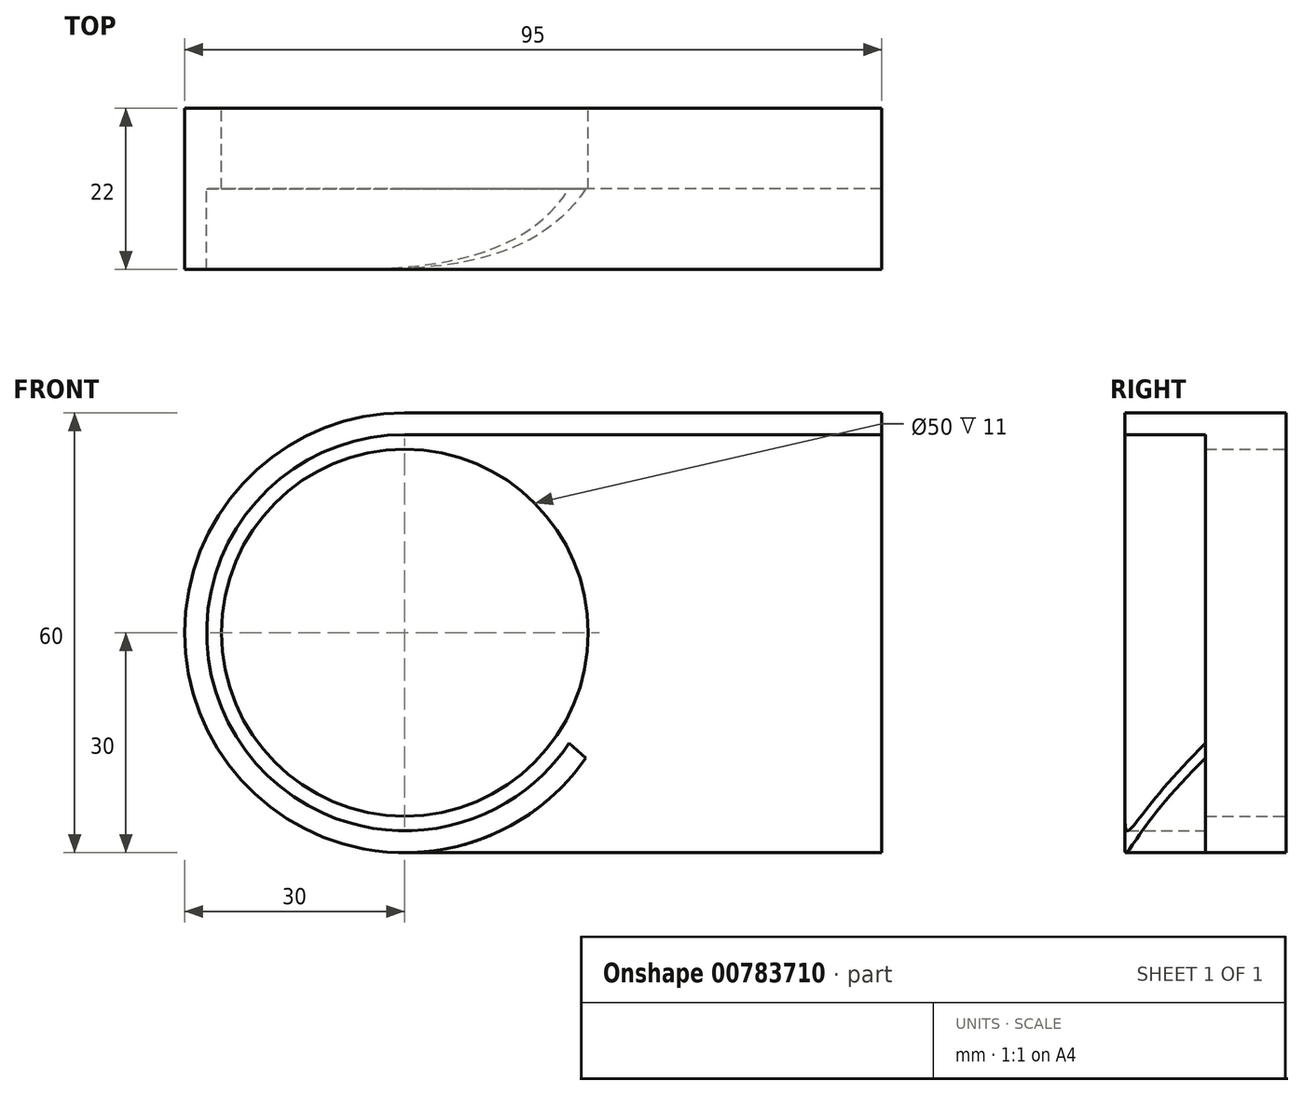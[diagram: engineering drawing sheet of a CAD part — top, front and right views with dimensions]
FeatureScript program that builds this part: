
annotation { "Feature Type Name" : "Feature", "Feature Type Description" : "" }
export const myFeature = defineFeature(function(context is Context, id is Id, definition is map)
    precondition{}
    {
        {
            var Q0;
            Q0=qCreatedBy(makeId("Front.planeOp"),FACE);
            var sketch = newSketch(context, id + "F0", { "sketchPlane" : qUnion([Q0])});
            skLineSegment(sketch, "E0.bottom", {"start": v(47.5, -30) * mm, "end": v(-17.5, -30) * mm});
            skLineSegment(sketch, "E0.top", {"start": v(47.5, 30) * mm, "end": v(-17.5, 30) * mm});
            skLineSegment(sketch, "E0.left", {"start": v(47.5, -30) * mm, "end": v(47.5, 30) * mm});
            skPoint(sketch, "E0.middle", {"position": v(0, 0) * mm});
            skCircle(sketch, "E1", {"center": v(-17.5, 0) * mm, "radius": 30 * mm});
            skPoint(sketch, "E1.first.point", {"position": v(-47.5, 0) * mm});
            skPoint(sketch, "E1.second.point", {"position": v(12.5, 0) * mm});
            skPoint(sketch, "E1.third.point", {"position": v(-17.5, -30) * mm});
            skPoint(sketch, "E2.orphan", {"position": v(-47.5, 30) * mm});
            skPoint(sketch, "E3.orphan", {"position": v(-47.5, -30) * mm});
            skCircle(sketch, "E4.0", {"center": v(-17.5, 0) * mm, "radius": 25 * mm});
            skSolve(sketch);
        }
        {
            var Q0;
            Q0=qSketchRegion(id+"F0",true);
            extrude(context, id + "F1", {"entities" : qUnion([Q0]), "depth" : 11 * mm, "offsetDistance" : 25 * mm});
        }
        {
            var Q0;
            Q0=makeQuery(id+"F1.opExtrude","CAP_FACE",FACE,{"disambiguationData":[OSD([sQuery(id+"F0.wireOp",EDGE,"E0.bottom"),sQuery(id+"F0.wireOp",EDGE,"E0.top"),sQuery(id+"F0.wireOp",EDGE,"E0.left"),sQuery(id+"F0.wireOp",EDGE,"E1"),sQuery(id+"F0.wireOp",EDGE,"E4.0")])],"isStart":true});
            var sketch = newSketch(context, id + "F2", { "sketchPlane" : qUnion([Q0])});
            skArc(sketch, "E5", {"start": v(17.5, -30) * mm, "mid": v(47.5, 0) * mm, "end": v(17.5, 30) * mm});
            skPoint(sketch, "E5.first.point", {"position": v(47.5, 0) * mm});
            skPoint(sketch, "E5.second.point", {"position": v(17.5, -30) * mm});
            skPoint(sketch, "E5.third.point", {"position": v(17.5, 30) * mm});
            skLineSegment(sketch, "E6.bottom", {"start": v(-47.5, 30) * mm, "end": v(17.51, 30) * mm});
            skLineSegment(sketch, "E6.top", {"start": v(-47.5, 27) * mm, "end": v(4.42, 27) * mm});
            skLineSegment(sketch, "E6.left", {"start": v(-47.5, 30) * mm, "end": v(-47.5, 27) * mm});
            skArc(sketch, "E7.0", {"start": v(-4.9, -15.08) * mm, "mid": v(41.34, -12.68) * mm, "end": v(17.5, 27) * mm});
            skLineSegment(sketch, "E8.trimOffspring", {"start": v(17.5, 27) * mm, "end": v(17.51, 27) * mm});
            skPoint(sketch, "E9.endSnap0", {"position": v(-15, -30) * mm});
            skLineSegment(sketch, "E10", {"start": v(4.42, 27) * mm, "end": v(17.51, 27) * mm});
            skArc(sketch, "E11", {"start": v(4.42, -27) * mm, "mid": v(10.8, -29.24) * mm, "end": v(17.5, -30) * mm});
            skPoint(sketch, "E9.end.orphan", {"position": v(-12.5, -30) * mm});
            skArc(sketch, "E12.trimOffspring", {"start": v(-7.14, -17.1) * mm, "mid": v(-2, -22.8) * mm, "end": v(4.42, -27) * mm});
            skLineSegment(sketch, "E13", {"start": v(-7.14, -17.1) * mm, "end": v(-4.9, -15.08) * mm});
            skSolve(sketch);
        }
        {
            var Q0;
            {var subQ5=sQuery(id+"F2.wireOp",EDGE,"E5");Q0=makeQuery(id+"F2.imprint","IMPRINT",FACE,{"disambiguationData":[TD([[makeQuery(id+"F2.imprint","IMPRINT",EDGE,{"derivedFrom":subQ5}),-1.0]])]});}
            extrude(context, id + "F3", {"entities" : qUnion([Q0]), "operationType" : NewBodyOperationType.ADD, "oppositeDirection" : true, "depth" : 22 * mm, "offsetDistance" : 25 * mm});
        }
        {
            var Q0;
            Q0=makeQuery(id+"F3.opExtrude","CAP_EDGE",EDGE,{"disambiguationData":[OSD([sQuery(id+"F2.wireOp",EDGE,"E13")])],"isStart":false});
            fillet(context, id + "F4", {"entities" : qUnion([Q0]), "radius" : 45 * mm, "tangentPropagation" : true, "allowEdgeOverflow" : false});
        }
    });
